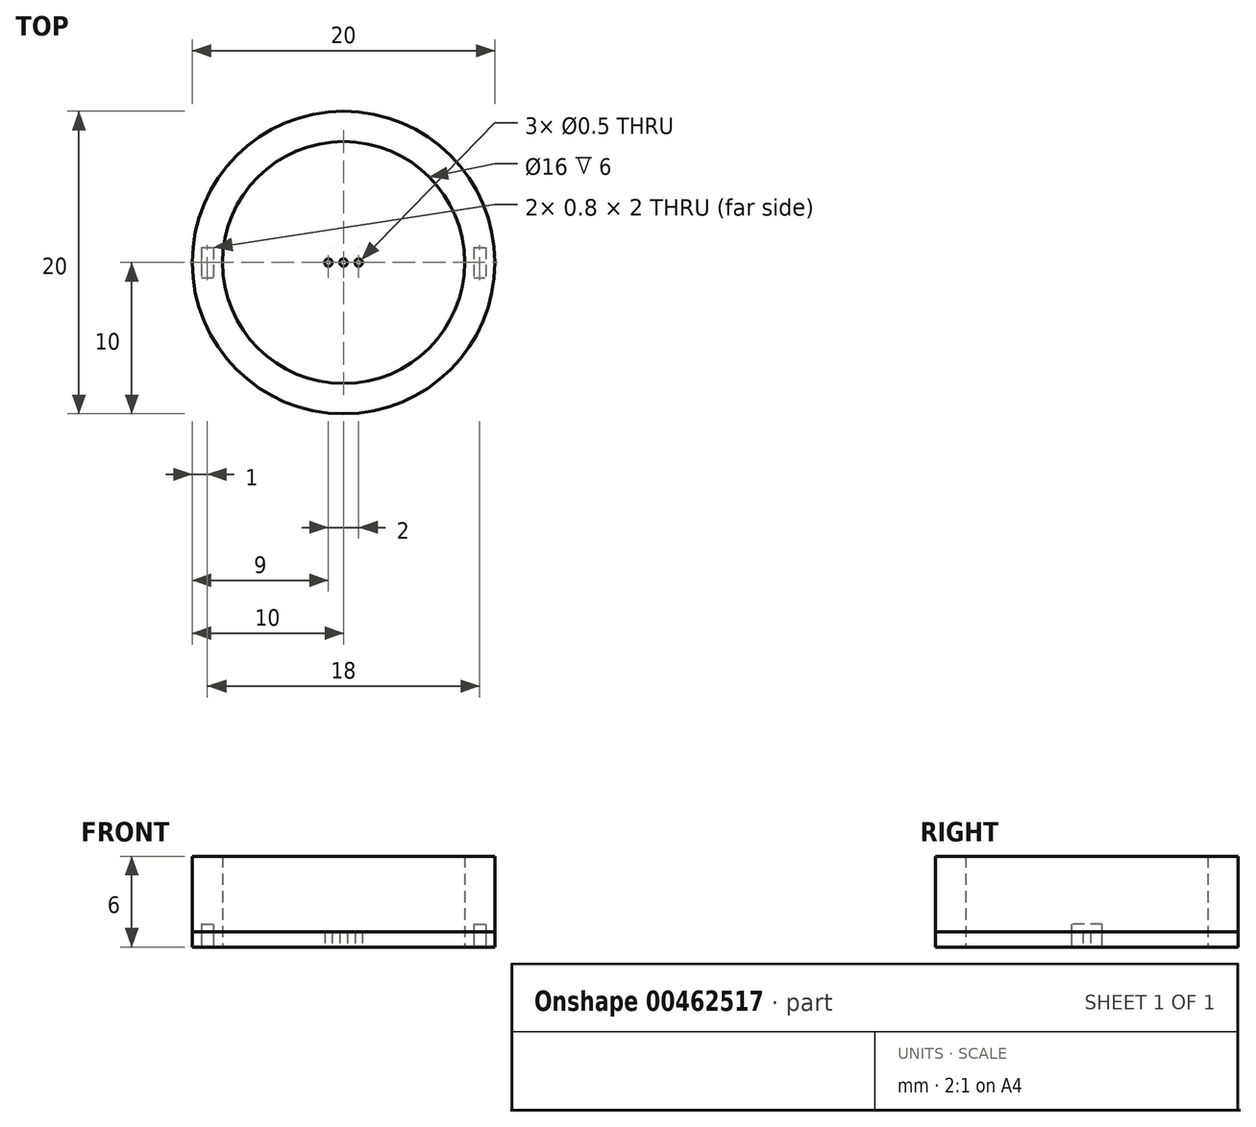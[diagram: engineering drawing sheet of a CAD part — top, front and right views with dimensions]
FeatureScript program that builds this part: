
annotation { "Feature Type Name" : "Feature", "Feature Type Description" : "" }
export const myFeature = defineFeature(function(context is Context, id is Id, definition is map)
    precondition{}
    {
        {
            var Q0;
            Q0=qCreatedBy(makeId("Top.planeOp"),FACE);
            var sketch = newSketch(context, id + "F0", { "sketchPlane" : qUnion([Q0])});
            skCircle(sketch, "E0", {"center": v(0, 0) * mm, "radius": 10 * mm});
            skCircle(sketch, "E1", {"center": v(0, 0) * mm, "radius": 8 * mm});
            skSolve(sketch);
        }
        {
            var Q0;
            Q0=qSketchRegion(id+"F0",true);
            extrude(context, id + "F1", {"entities" : qUnion([Q0]), "depth" : 6 * mm});
        }
        {
            var Q0;
            Q0=qCreatedBy(makeId("Top.planeOp"),FACE);
            var sketch = newSketch(context, id + "F2", { "sketchPlane" : qUnion([Q0])});
            skCircle(sketch, "E2", {"center": v(0, 0) * mm, "radius": 10 * mm});
            skCircle(sketch, "E3", {"center": v(0, 0) * mm, "radius": 0.25 * mm});
            skCircle(sketch, "E4", {"center": v(1, 0) * mm, "radius": 0.25 * mm});
            skCircle(sketch, "E5", {"center": v(-1, 0) * mm, "radius": 0.25 * mm});
            skLineSegment(sketch, "E6.bottom", {"start": v(-9.4, 1) * mm, "end": v(-8.6, 1) * mm});
            skLineSegment(sketch, "E6.top", {"start": v(-9.4, -1) * mm, "end": v(-8.6, -1) * mm});
            skLineSegment(sketch, "E6.left", {"start": v(-9.4, 1) * mm, "end": v(-9.4, -1) * mm});
            skLineSegment(sketch, "E6.right", {"start": v(-8.6, 1) * mm, "end": v(-8.6, -1) * mm});
            skLineSegment(sketch, "E7.bottom", {"start": v(8.6, 1) * mm, "end": v(9.4, 1) * mm});
            skLineSegment(sketch, "E7.top", {"start": v(8.6, -1) * mm, "end": v(9.4, -1) * mm});
            skLineSegment(sketch, "E7.left", {"start": v(8.6, 1) * mm, "end": v(8.6, -1) * mm});
            skLineSegment(sketch, "E7.right", {"start": v(9.4, 1) * mm, "end": v(9.4, -1) * mm});
            skSolve(sketch);
        }
        {
            var Q0;
            Q0=qSketchRegion(id+"F2",true);
            extrude(context, id + "F3", {"entities" : qUnion([Q0]), "depth" : 1 * mm});
        }
        {
            var Q0;
            Q0=makeQuery(id+"F2.imprint","IMPRINT",FACE,{"disambiguationData":[TD([[makeQuery(id+"F2.imprint","IMPRINT",EDGE,{"derivedFrom":sQuery(id+"F2.wireOp",EDGE,"E7.bottom")}),-1.0]])]});
            var Q1;
            Q1=makeQuery(id+"F2.imprint","IMPRINT",FACE,{"disambiguationData":[TD([[makeQuery(id+"F2.imprint","IMPRINT",EDGE,{"derivedFrom":sQuery(id+"F2.wireOp",EDGE,"E6.bottom")}),-1.0]])]});
            extrude(context, id + "F4", {"entities" : qUnion([Q0, Q1]), "operationType" : NewBodyOperationType.REMOVE, "depth" : 1.5 * mm});
        }
    });
